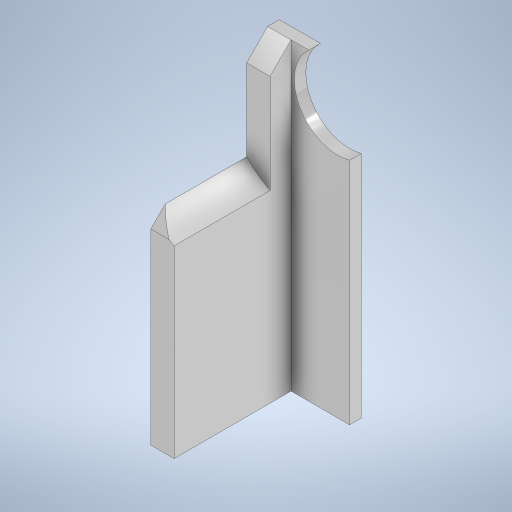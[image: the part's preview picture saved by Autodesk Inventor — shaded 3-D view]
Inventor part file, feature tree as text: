
AUTODESK INVENTOR PART (.ipt)
format: ipt  version: 2024 (Build 280153000, 153)  size: 257,536 bytes
history: native  units: mm
features: extrude x4, sketch x4, chamfer x1
ambient origin geometry x8: Origin, YZ Plane, XZ Plane, XY Plane, X Axis, Y Axis, Z Axis, Center Point
bodies: Solid1 (feature_tree)
feature tree (9):
  extrude  "Extrusion1"  Depth=20.0mm
  chamfer  "Chamfer1"  Distance=260.0mm
  extrude  "Extrusion2"  Depth=10.0mm
  extrude  "Extrusion4"  Depth=82.0mm TaperAngle=0.0deg
  extrude  "Extrusion5"  Depth=82.0mm TaperAngle=0.0deg
  sketch  "Sketch1"  dims[d0=110.0mm d1=20.0mm]
  sketch  "Sketch2"  dims[d3=60.0mm d4=260.0mm d5=0.0mm]
  sketch  "Sketch4"  dims[d6=100.0mm d7=2.0mm d8=45.0deg d9=10.0mm]
  sketch  "Sketch5"  dims[d10=50.0mm d11=0.0mm d18=82.0mm d19=0.0mm d20=82.0mm d21=0.0mm]
